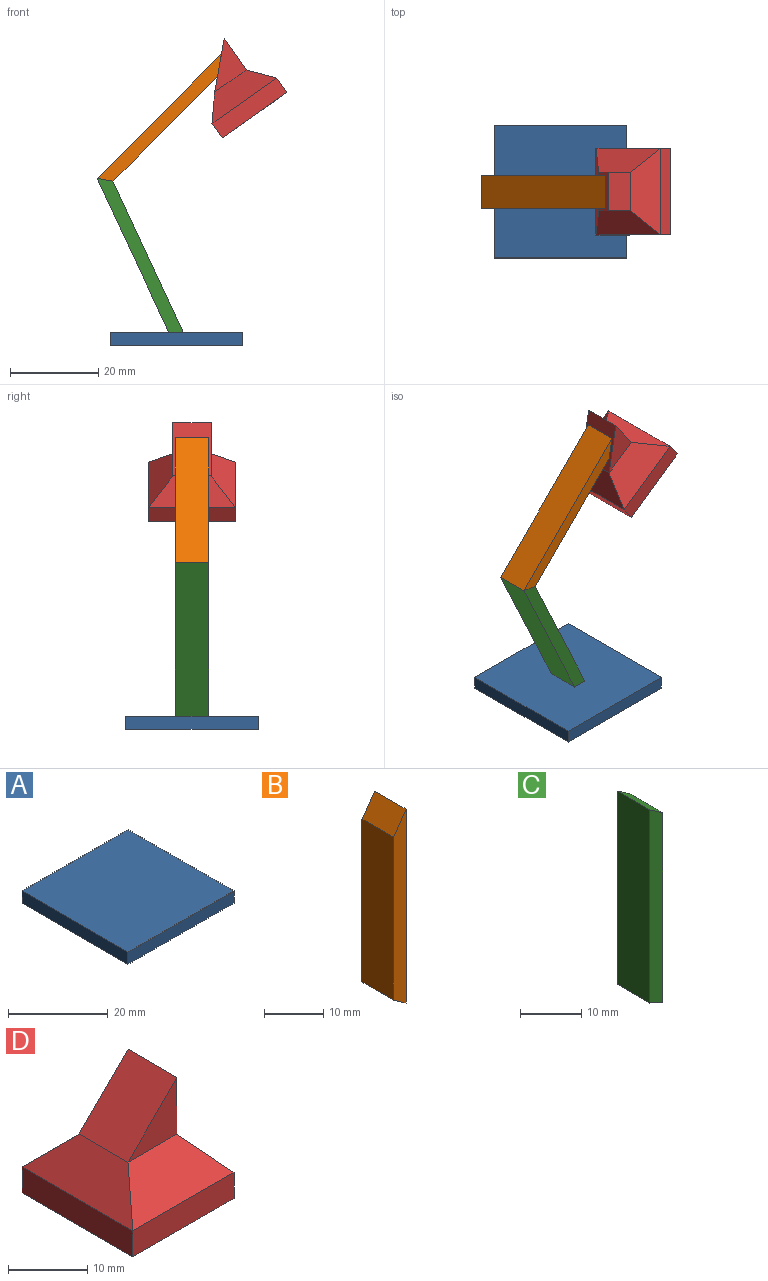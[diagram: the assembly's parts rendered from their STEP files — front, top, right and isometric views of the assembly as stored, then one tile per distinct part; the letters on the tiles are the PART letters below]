
ASSEMBLY  parts=4 mates=3
PART A: 6 faces, bbox 30x30x3 mm
  f0: plane 30x3mm, normal (0,1,0), area 90mm2, adj f1,f3,f4,f5
  f1: plane 30x3mm, normal (-1,0,0), area 90mm2, adj f0,f2,f4,f5
  f2: plane 30x3mm, normal (0,-1,0), area 90mm2, adj f1,f3,f4,f5
  f3: plane 30x3mm, normal (1,0,0), area 90mm2, adj f0,f2,f4,f5
  f4: plane 30x30mm, normal (0,0,1), area 900mm2, adj f0,f1,f2,f3
  f5: plane 30x30mm, normal (0,0,-1), area 900mm2, adj f0,f1,f2,f3
PART B: 6 faces, bbox 3x7.5x40 mm
  f0: plane 33.62x7.5mm, normal (-1,0,0), area 252.1mm2, adj f1,f3,f4,f5
  f1: plane 7.5x3mm, normal (-0.57,0,-0.82), area 27.5mm2, adj f0,f2,f4,f5
  f2: plane 40x7.5mm, normal (1,0,0), area 300mm2, adj f1,f3,f4,f5
  f3: plane 7.5x4.28mm, normal (-0.82,0,0.57), area 39.2mm2, adj f0,f2,f4,f5
  f4: plane 40x3mm, normal (0,-1,0), area 110.4mm2, adj f0,f1,f2,f3
  f5: plane 40x3mm, normal (0,1,0), area 110.4mm2, adj f0,f1,f2,f3
PART C: 6 faces, bbox 3x7.5x40 mm
  f0: plane 38.6x7.5mm, normal (-1,0,0), area 289.5mm2, adj f1,f3,f4,f5
  f1: plane 7.5x3mm, normal (-0.42,0,-0.91), area 24.8mm2, adj f0,f2,f4,f5
  f2: plane 37.9x7.5mm, normal (1,0,0), area 284.2mm2, adj f1,f3,f4,f5
  f3: plane 7.5x3mm, normal (0.57,0,0.82), area 27.5mm2, adj f0,f2,f4,f5
  f4: plane 40x3mm, normal (0,-1,0), area 114.8mm2, adj f0,f1,f2,f3
  f5: plane 40x3mm, normal (0,1,0), area 114.8mm2, adj f0,f1,f2,f3
PART D: 15 faces, bbox 18x19.7x18.2 mm
  f0: plane 8.72x8.72mm, normal (-0.71,0,0.71), area 107.5mm2, adj f1,f3,f4,f5
  f1: plane 19.72x5.5mm, normal (-0.76,0,0.64), area 102.3mm2, adj f0,f6,f11,f12
  f2: plane 19.72x5.5mm, normal (0.76,0,0.64), area 102.3mm2, adj f3,f8,f11,f12
  f3: plane 8.72x8.72mm, normal (1,0,0), area 76mm2, adj f0,f2,f4,f5
  f4: plane 8.72x8.72mm, normal (0,-1,0), area 38mm2, adj f0,f3,f12
  f5: plane 8.72x8.72mm, normal (0,1,0), area 38mm2, adj f0,f3,f11
  f6: plane 19.72x4mm, normal (-1,0,0), area 78.9mm2, adj f1,f7,f9,f10
  f7: plane 19.72x18mm, normal (0,0,-1), area 316.4mm2, adj f6,f8,f9,f10,f13
  f8: plane 19.72x4mm, normal (1,0,0), area 78.9mm2, adj f2,f7,f9,f10
  f9: plane 18x4mm, normal (0,-1,0), area 72mm2, adj f6,f7,f8,f12
  f10: plane 18x4mm, normal (0,1,0), area 72mm2, adj f6,f7,f8,f11
  f11: plane 18x5.5mm, normal (0,0.71,0.71), area 103.9mm2, adj f1,f2,f5,f10
  f12: plane 18x5.5mm, normal (0,-0.71,0.71), area 103.9mm2, adj f1,f2,f4,f9
  f13: cylinder r=3.5mm len=9mm, axis (0,0,-1), area 197.9mm2, adj f7,f14
  f14: plane 7x7mm, normal (0,0,-1), area 38.5mm2, adj f13
PLACE A t=(-362.2,-58.21,239.47)mm
PLACE B rot(axis=(0.38,0,0.92),180deg) t=(-377.54,-61.96,292.97)mm
PLACE C rot(axis=(0,-1,0),25deg) t=(-385.36,-54.46,259.96)mm
PLACE D rot(axis=(0,-1,0),35deg) t=(-367.8,-58.21,300.58)mm
MATE fastened D.f0 <-> B.f3  axis (-0.98,0,0.17) through (-367.34,-58.21,303.17)mm
MATE fastened B.f1 <-> C.f3  axis (-0.17,0,-0.98) through (-393.37,-58.21,277.14)mm
MATE fastened C.f1 <-> A.f4  axis (0,0,-1) through (-377.2,-58.21,242.47)mm
